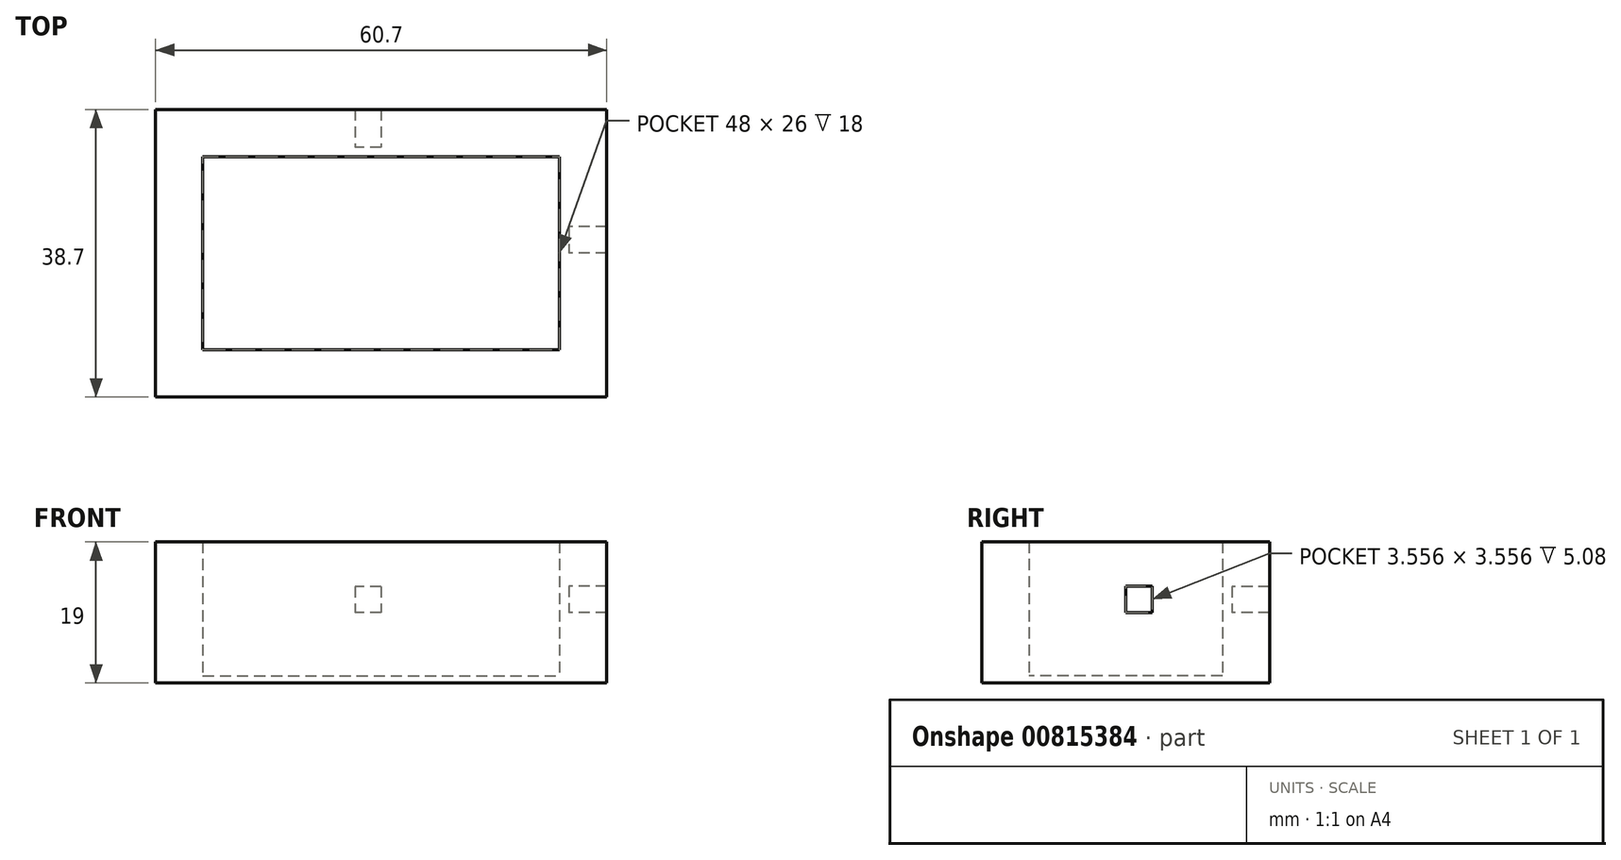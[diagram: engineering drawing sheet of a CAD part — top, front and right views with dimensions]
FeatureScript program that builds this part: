
annotation { "Feature Type Name" : "Feature", "Feature Type Description" : "" }
export const myFeature = defineFeature(function(context is Context, id is Id, definition is map)
    precondition{}
    {
        {
            var Q0;
            Q0=qCreatedBy(makeId("Top.planeOp"),FACE);
            var sketch = newSketch(context, id + "F0", { "sketchPlane" : qUnion([Q0])});
            skLineSegment(sketch, "E0.bottom", {"start": v(-24, 13) * mm, "end": v(24, 13) * mm});
            skLineSegment(sketch, "E0.top", {"start": v(-24, -13) * mm, "end": v(24, -13) * mm});
            skLineSegment(sketch, "E0.left", {"start": v(-24, 13) * mm, "end": v(-24, -13) * mm});
            skLineSegment(sketch, "E0.right", {"start": v(24, 13) * mm, "end": v(24, -13) * mm});
            skPoint(sketch, "E0.middle", {"position": v(0, 0) * mm});
            skLineSegment(sketch, "E1.bottom", {"start": v(-25.27, 14.27) * mm, "end": v(25.27, 14.27) * mm});
            skLineSegment(sketch, "E1.top", {"start": v(-25.27, -14.27) * mm, "end": v(25.27, -14.27) * mm});
            skLineSegment(sketch, "E1.left", {"start": v(-25.27, 14.27) * mm, "end": v(-25.27, -14.27) * mm});
            skLineSegment(sketch, "E1.right", {"start": v(25.27, 14.27) * mm, "end": v(25.27, -14.27) * mm});
            skLineSegment(sketch, "E2", {"start": v(-24, 13) * mm, "end": v(-25.27, 13) * mm});
            skLineSegment(sketch, "E3", {"start": v(24, 13) * mm, "end": v(25.27, 13) * mm});
            skLineSegment(sketch, "E4", {"start": v(24, -13) * mm, "end": v(25.27, -13) * mm});
            skLineSegment(sketch, "E5", {"start": v(-24, -13) * mm, "end": v(-25.27, -13) * mm});
            skLineSegment(sketch, "E6", {"start": v(-24, 13) * mm, "end": v(-24, 14.27) * mm});
            skLineSegment(sketch, "E7", {"start": v(24, 13) * mm, "end": v(24, 14.27) * mm});
            skLineSegment(sketch, "E8", {"start": v(24, -13) * mm, "end": v(24, -14.27) * mm});
            skLineSegment(sketch, "E9", {"start": v(-24, -13) * mm, "end": v(-24, -14.27) * mm});
            skSolve(sketch);
        }
        {
            var Q0;
            Q0=makeQuery(id+"F0.imprint","IMPRINT",FACE,{"disambiguationData":[TD([[makeQuery(id+"F0.imprint","IMPRINT",EDGE,{"derivedFrom":sQuery(id+"F0.wireOp",EDGE,"E0.bottom")}),-1.0]])]});
            extrude(context, id + "F1", {"entities" : qUnion([Q0]), "depth" : 1 * mm, "offsetDistance" : 25.4 * mm});
        }
        {
            var Q0;
            Q0=makeQuery(id+"F0.imprint","IMPRINT",FACE,{"disambiguationData":[TD([[makeQuery(id+"F0.imprint","IMPRINT",EDGE,{"derivedFrom":sQuery(id+"F0.wireOp",EDGE,"E0.top")}),-1.0]])]});
            var Q1;
            Q1=makeQuery(id+"F0.imprint","IMPRINT",FACE,{"disambiguationData":[TD([[makeQuery(id+"F0.imprint","IMPRINT",EDGE,{"derivedFrom":sQuery(id+"F0.wireOp",EDGE,"E0.bottom")}),1.0]])]});
            var Q2;
            Q2=makeQuery(id+"F0.imprint","IMPRINT",FACE,{"disambiguationData":[TD([[makeQuery(id+"F0.imprint","IMPRINT",EDGE,{"derivedFrom":sQuery(id+"F0.wireOp",EDGE,"E0.right")}),1.0]])]});
            var Q3;
            Q3=makeQuery(id+"F0.imprint","IMPRINT",FACE,{"disambiguationData":[TD([[makeQuery(id+"F0.imprint","IMPRINT",EDGE,{"derivedFrom":sQuery(id+"F0.wireOp",EDGE,"E0.left")}),-1.0]])]});
            var Q4;
            {var subQ4=sQuery(id+"F0.wireOp",EDGE,"E5");Q4=makeQuery(id+"F0.imprint","IMPRINT",FACE,{"disambiguationData":[TD([[makeQuery(id+"F0.imprint","IMPRINT",EDGE,{"derivedFrom":subQ4}),1.0]])]});}
            var Q5;
            {var subQ4=sQuery(id+"F0.wireOp",EDGE,"E4");Q5=makeQuery(id+"F0.imprint","IMPRINT",FACE,{"disambiguationData":[TD([[makeQuery(id+"F0.imprint","IMPRINT",EDGE,{"derivedFrom":subQ4}),-1.0]])]});}
            var Q6;
            {var subQ4=sQuery(id+"F0.wireOp",EDGE,"E3");Q6=makeQuery(id+"F0.imprint","IMPRINT",FACE,{"disambiguationData":[TD([[makeQuery(id+"F0.imprint","IMPRINT",EDGE,{"derivedFrom":subQ4}),1.0]])]});}
            var Q7;
            {var subQ4=sQuery(id+"F0.wireOp",EDGE,"E2");Q7=makeQuery(id+"F0.imprint","IMPRINT",FACE,{"disambiguationData":[TD([[makeQuery(id+"F0.imprint","IMPRINT",EDGE,{"derivedFrom":subQ4}),-1.0]])]});}
            extrude(context, id + "F2", {"entities" : qUnion([Q0, Q1, Q2, Q3, Q4, Q5, Q6, Q7]), "operationType" : NewBodyOperationType.ADD, "depth" : 19 * mm, "offsetDistance" : 25.4 * mm});
        }
        {
            var Q0;
            Q0=makeQuery(id+"F2.opExtrude","SWEPT_FACE",FACE,{"disambiguationData":[OSD([sQuery(id+"F0.wireOp",EDGE,"E1.top")])]});
            var sketch = newSketch(context, id + "F3", { "sketchPlane" : qUnion([Q0])});
            skPoint(sketch, "E10.middle.positionSnap0", {"position": v(-25.27, 9.5) * mm});
            skPoint(sketch, "E10.centerSnap0", {"position": v(-25.27, 9.5) * mm});
            skLineSegment(sketch, "E11.left", {"start": v(0, 13) * mm, "end": v(0, 9.5) * mm});
            skLineSegment(sketch, "E12.MirrorCS", {"start": v(0, 13) * mm, "end": v(-3.5, 13) * mm});
            skLineSegment(sketch, "E13.MirrorCS", {"start": v(-3.56, 13) * mm, "end": v(-3.56, 9.5) * mm});
            skLineSegment(sketch, "E14.MirrorCS", {"start": v(0, 9.5) * mm, "end": v(-3.56, 9.5) * mm});
            skSolve(sketch);
        }
        {
            var Q0;
            Q0=makeQuery(id+"F2.opExtrude","SWEPT_FACE",FACE,{"disambiguationData":[OSD([sQuery(id+"F0.wireOp",EDGE,"E1.bottom")])]});
            var sketch = newSketch(context, id + "F4", { "sketchPlane" : qUnion([Q0])});
            skPoint(sketch, "E15", {"position": v(25.27, 9.5) * mm});
            skPoint(sketch, "E16", {"position": v(0, 0) * mm});
            skLineSegment(sketch, "E17.bottom", {"start": v(0, 13) * mm, "end": v(3.5, 13) * mm});
            skLineSegment(sketch, "E17.top", {"start": v(0, 9.5) * mm, "end": v(3.5, 9.5) * mm});
            skLineSegment(sketch, "E17.left", {"start": v(0, 13) * mm, "end": v(0, 9.5) * mm});
            skLineSegment(sketch, "E17.right", {"start": v(3.5, 13) * mm, "end": v(3.5, 9.5) * mm});
            skSolve(sketch);
        }
        {
            var Q0;
            Q0=makeQuery(id+"F4.imprint","IMPRINT",FACE,{"disambiguationData":[TD([[makeQuery(id+"F4.imprint","IMPRINT",EDGE,{"derivedFrom":sQuery(id+"F4.wireOp",EDGE,"E17.bottom")}),1.0]])]});
            extrude(context, id + "F5", {"entities" : qUnion([Q0]), "operationType" : NewBodyOperationType.ADD, "depth" : 5.08 * mm, "offsetDistance" : 25.4 * mm});
        }
        {
            var Q0;
            {var subQ0=sQuery(id+"F0.wireOp",EDGE,"E1.top");Q0=makeQuery(id+"F3.imprint","IMPRINT",FACE,{"disambiguationData":[TD([[makeQuery(id+"F3.imprint","IMPRINT",EDGE,{"derivedFrom":makeQuery(id+"F2.opExtrude","CAP_EDGE",EDGE,{"disambiguationData":[OSD([subQ0])],"isStart":true})}),1.0]])]});}
            extrude(context, id + "F6", {"entities" : qUnion([Q0]), "operationType" : NewBodyOperationType.ADD, "depth" : 5.08 * mm, "offsetDistance" : 25.4 * mm});
        }
        {
            var Q0;
            {var subQ0=sQuery(id+"F0.wireOp",EDGE,"E1.right");Q0=makeQuery(id+"F6.boolean.opBoolean","MERGE",FACE,{"derivedFrom":[makeQuery(id+"F5.boolean.opBoolean","MERGE",FACE,{"derivedFrom":[makeQuery(id+"F2.opExtrude","SWEPT_FACE",FACE,{"disambiguationData":[OSD([subQ0])]}),makeQuery(id+"F5.opExtrude","SWEPT_FACE",FACE,{"disambiguationData":[OSD([sQuery(id+"F0.wireOp",EDGE,"E1.bottom"),subQ0])]})]}),makeQuery(id+"F6.opExtrude","SWEPT_FACE",FACE,{"disambiguationData":[OSD([sQuery(id+"F0.wireOp",EDGE,"E1.top"),subQ0])]})]});}
            var sketch = newSketch(context, id + "F7", { "sketchPlane" : qUnion([Q0])});
            skLineSegment(sketch, "E18.left", {"start": v(3.56, 13.06) * mm, "end": v(3.56, 9.5) * mm});
            skLineSegment(sketch, "E19.MirrorCS", {"start": v(3.56, 13.06) * mm, "end": v(0, 13.06) * mm});
            skLineSegment(sketch, "E20.MirrorCS", {"start": v(0, 13.06) * mm, "end": v(0, 9.5) * mm});
            skLineSegment(sketch, "E21.MirrorCS", {"start": v(3.56, 9.5) * mm, "end": v(0, 9.5) * mm});
            skPoint(sketch, "E22", {"position": v(19.35, 9.5) * mm});
            skSolve(sketch);
        }
        {
            var Q0;
            {var subQ0=sQuery(id+"F0.wireOp",EDGE,"E1.left");Q0=makeQuery(id+"F6.boolean.opBoolean","MERGE",FACE,{"derivedFrom":[makeQuery(id+"F5.boolean.opBoolean","MERGE",FACE,{"derivedFrom":[makeQuery(id+"F2.opExtrude","SWEPT_FACE",FACE,{"disambiguationData":[OSD([subQ0])]}),makeQuery(id+"F5.opExtrude","SWEPT_FACE",FACE,{"disambiguationData":[OSD([sQuery(id+"F0.wireOp",EDGE,"E1.bottom"),subQ0])]})]}),makeQuery(id+"F6.opExtrude","SWEPT_FACE",FACE,{"disambiguationData":[OSD([sQuery(id+"F0.wireOp",EDGE,"E1.top"),subQ0])]})]});}
            var sketch = newSketch(context, id + "F8", { "sketchPlane" : qUnion([Q0])});
            skLineSegment(sketch, "E23.MirrorCS", {"start": v(0, 13) * mm, "end": v(0, 9.5) * mm});
            skPoint(sketch, "E24", {"position": v(0, 0) * mm});
            skPoint(sketch, "E25", {"position": v(19.35, 9.5) * mm});
            skLineSegment(sketch, "E26.MirrorCS", {"start": v(-3.56, 13.06) * mm, "end": v(-0.06, 13.06) * mm});
            skLineSegment(sketch, "E27.MirrorCS", {"start": v(-3.56, 13.06) * mm, "end": v(-3.56, 9.5) * mm});
            skLineSegment(sketch, "E28.MirrorCS", {"start": v(-3.56, 9.5) * mm, "end": v(0, 9.5) * mm});
            skSolve(sketch);
        }
        {
            var Q0;
            Q0=makeQuery(id+"F7.imprint","IMPRINT",FACE,{"disambiguationData":[TD([[makeQuery(id+"F7.imprint","IMPRINT",EDGE,{"derivedFrom":sQuery(id+"F7.wireOp",EDGE,"E18.left")}),1.0]])]});
            extrude(context, id + "F9", {"entities" : qUnion([Q0]), "operationType" : NewBodyOperationType.ADD, "depth" : 5.08 * mm, "offsetDistance" : 25.4 * mm});
        }
        {
            var Q0;
            {var subQ0=sQuery(id+"F0.wireOp",EDGE,"E1.left");var subQ1=sQuery(id+"F0.wireOp",EDGE,"E1.bottom");Q0=makeQuery(id+"F8.imprint","IMPRINT",FACE,{"disambiguationData":[TD([[makeQuery(id+"F8.imprint","IMPRINT",EDGE,{"derivedFrom":makeQuery(id+"F5.opExtrude","CAP_EDGE",EDGE,{"disambiguationData":[OSD([subQ1,subQ0])],"isStart":false})}),1.0]])]});}
            extrude(context, id + "F10", {"entities" : qUnion([Q0]), "operationType" : NewBodyOperationType.ADD, "depth" : 5.08 * mm, "offsetDistance" : 25.4 * mm});
        }
    });
